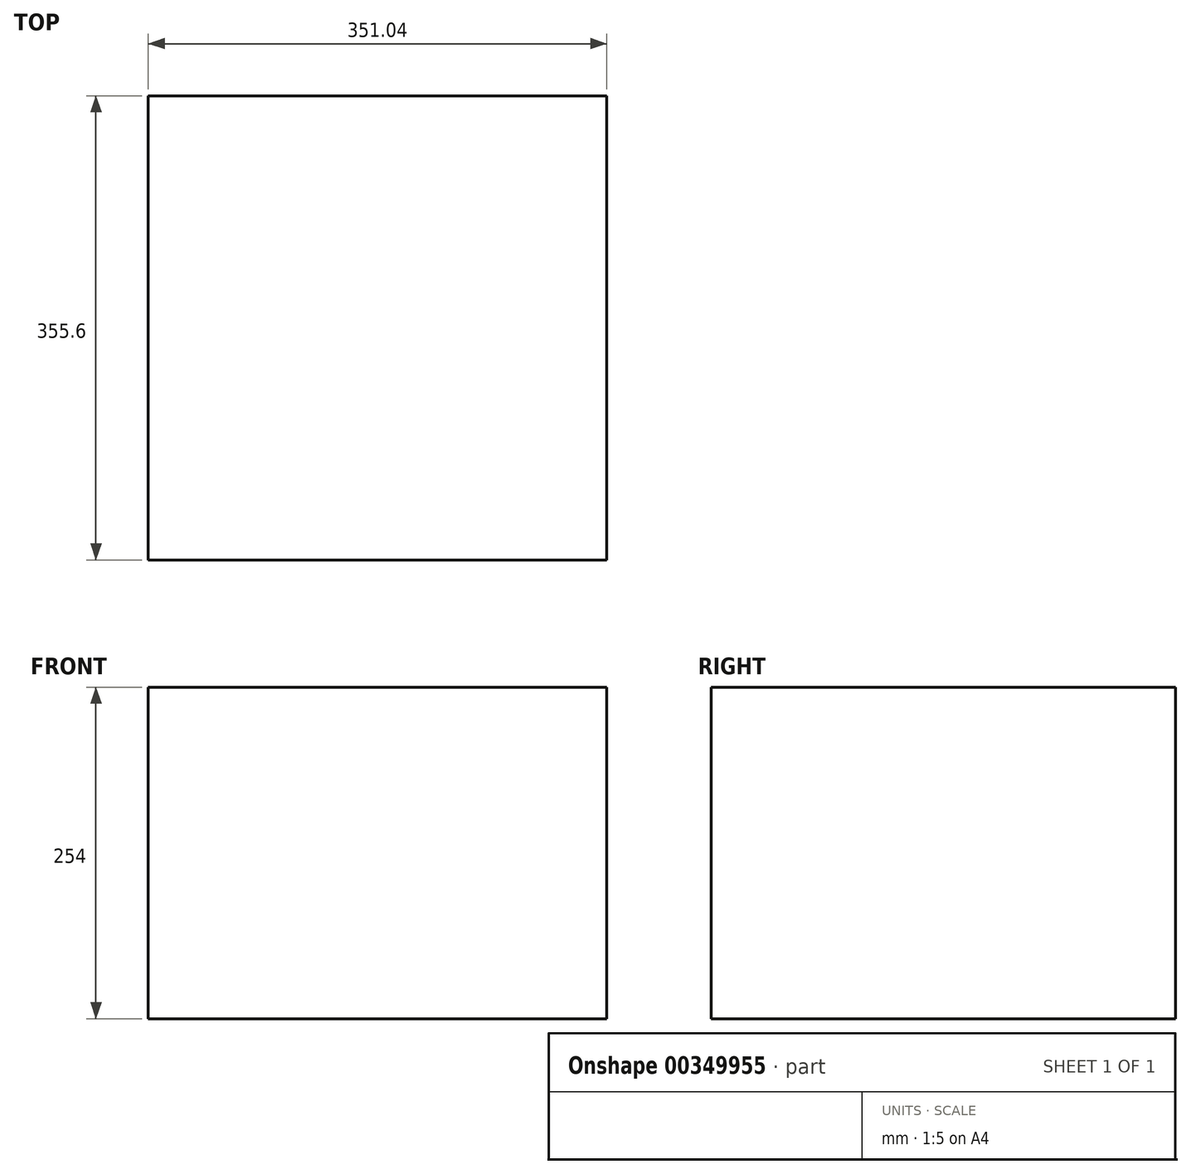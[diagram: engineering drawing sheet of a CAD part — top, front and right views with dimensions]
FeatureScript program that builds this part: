
annotation { "Feature Type Name" : "Feature", "Feature Type Description" : "" }
export const myFeature = defineFeature(function(context is Context, id is Id, definition is map)
    precondition{}
    {
        {
            var Q0;
            Q0=qCreatedBy(makeId("Front.planeOp"),FACE);
            var sketch = newSketch(context, id + "F0", { "sketchPlane" : qUnion([Q0])});
            skLineSegment(sketch, "E0.bottom", {"start": v(-174.74, 129.08) * mm, "end": v(176.3, 129.08) * mm});
            skLineSegment(sketch, "E0.top", {"start": v(-174.74, -124.92) * mm, "end": v(176.3, -124.92) * mm});
            skLineSegment(sketch, "E0.left", {"start": v(-174.74, 129.08) * mm, "end": v(-174.74, -124.92) * mm});
            skLineSegment(sketch, "E0.right", {"start": v(176.3, 129.08) * mm, "end": v(176.3, -124.92) * mm});
            skSolve(sketch);
        }
        {
            var Q0;
            Q0 = qSketchRegion(id + "F0", true);
            extrude(context, id + "F1", {"entities" : qUnion([Q0]), "depth" : 355.6 * mm});
        }
    });
